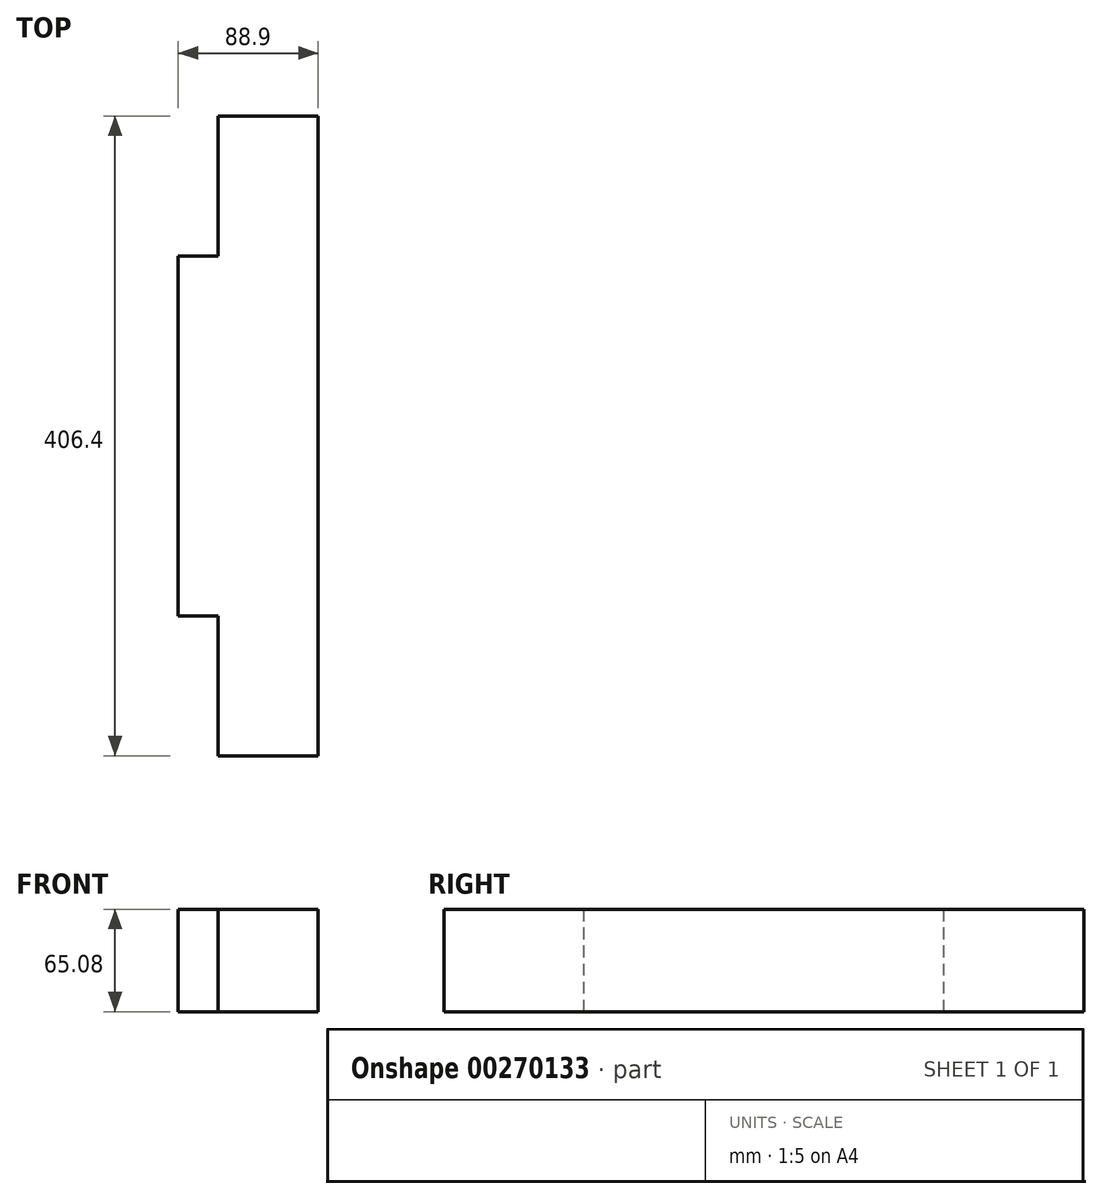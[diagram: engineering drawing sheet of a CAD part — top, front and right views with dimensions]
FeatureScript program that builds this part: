
annotation { "Feature Type Name" : "Feature", "Feature Type Description" : "" }
export const myFeature = defineFeature(function(context is Context, id is Id, definition is map)
    precondition{}
    {
        {
            var Q0;
            Q0=qCreatedBy(makeId("Right.planeOp"),FACE);
            var sketch = newSketch(context, id + "F0", { "sketchPlane" : qUnion([Q0])});
            skLineSegment(sketch, "E0.bottom", {"start": v(203.2, -32.54) * mm, "end": v(-203.2, -32.54) * mm});
            skLineSegment(sketch, "E0.top", {"start": v(203.2, 32.54) * mm, "end": v(-203.2, 32.54) * mm});
            skLineSegment(sketch, "E0.left", {"start": v(203.2, -32.54) * mm, "end": v(203.2, 32.54) * mm});
            skLineSegment(sketch, "E0.right", {"start": v(-203.2, -32.54) * mm, "end": v(-203.2, 32.54) * mm});
            skPoint(sketch, "E0.middle", {"position": v(0, 0) * mm});
            skSolve(sketch);
        }
        {
            var Q0;
            Q0=makeQuery(id+"F0.imprint","IMPRINT",FACE,{"disambiguationData":[TD([[makeQuery(id+"F0.imprint","IMPRINT",EDGE,{"derivedFrom":sQuery(id+"F0.wireOp",EDGE,"E0.bottom")}),-1.0]])]});
            extrude(context, id + "F1", {"entities" : qUnion([Q0]), "depth" : 88.9 * mm});
        }
        {
            var Q0;
            Q0=makeQuery(id+"F1.opExtrude","SWEPT_FACE",FACE,{"disambiguationData":[OSD([sQuery(id+"F0.wireOp",EDGE,"E0.top")])]});
            var sketch = newSketch(context, id + "F2", { "sketchPlane" : qUnion([Q0])});
            skLineSegment(sketch, "E1.bottom", {"start": v(0, 203.2) * mm, "end": v(25.4, 203.2) * mm});
            skLineSegment(sketch, "E1.top", {"start": v(0, 114.3) * mm, "end": v(25.4, 114.3) * mm});
            skLineSegment(sketch, "E1.left", {"start": v(0, 203.2) * mm, "end": v(0, 114.3) * mm});
            skLineSegment(sketch, "E1.right", {"start": v(25.4, 203.2) * mm, "end": v(25.4, 114.3) * mm});
            skLineSegment(sketch, "E2.bottom", {"start": v(0, -203.2) * mm, "end": v(25.4, -203.2) * mm});
            skLineSegment(sketch, "E2.top", {"start": v(0, -114.3) * mm, "end": v(25.4, -114.3) * mm});
            skLineSegment(sketch, "E2.left", {"start": v(0, -203.2) * mm, "end": v(0, -114.3) * mm});
            skLineSegment(sketch, "E2.right", {"start": v(25.4, -203.2) * mm, "end": v(25.4, -114.3) * mm});
            skSolve(sketch);
        }
        {
            var Q0;
            Q0=makeQuery(id+"F2.imprint","IMPRINT",FACE,{"disambiguationData":[TD([[makeQuery(id+"F2.imprint","IMPRINT",EDGE,{"derivedFrom":sQuery(id+"F2.wireOp",EDGE,"E1.bottom")}),1.0]])]});
            var Q1;
            Q1=makeQuery(id+"F2.imprint","IMPRINT",FACE,{"disambiguationData":[TD([[makeQuery(id+"F2.imprint","IMPRINT",EDGE,{"derivedFrom":sQuery(id+"F2.wireOp",EDGE,"E2.bottom")}),-1.0]])]});
            extrude(context, id + "F3", {"entities" : qUnion([Q0, Q1]), "operationType" : NewBodyOperationType.REMOVE, "endBound" : BoundingType.THROUGH_ALL, "oppositeDirection" : true, "depth" : 25.4 * mm});
        }
    });
